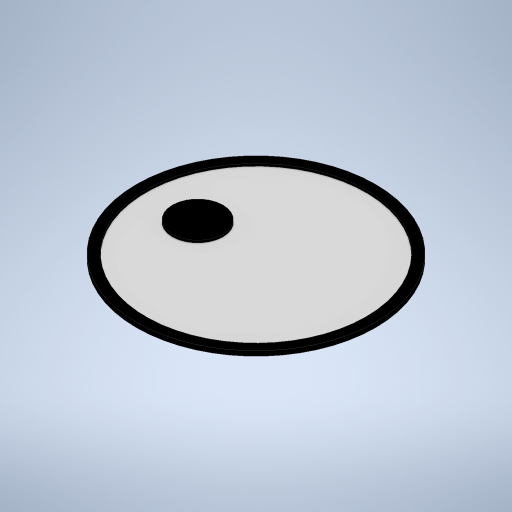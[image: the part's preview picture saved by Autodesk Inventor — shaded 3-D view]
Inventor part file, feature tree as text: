
AUTODESK INVENTOR PART (.ipt)
format: ipt  version: 2023 (Build 270158000, 158)  size: 240,128 bytes
history: native  units: mm
features: extrude x2, sketch x2, other x1, projected_geometry x1
ambient origin geometry x8: Origin, YZ Plane, XZ Plane, XY Plane, X Axis, Y Axis, Z Axis, Center Point
bodies: Body1 (feature_tree)
feature tree (6):
  other  "Bryła1"
  extrude  "Wyciągnięcie proste1"  Depth=10.0mm
  extrude  "Wyciągnięcie proste2"  Depth=0.1mm TaperAngle=0.0deg
  sketch  "Szkic1"
  sketch  "Szkic2"
  projected_geometry  "Pętla rzutowana1"
